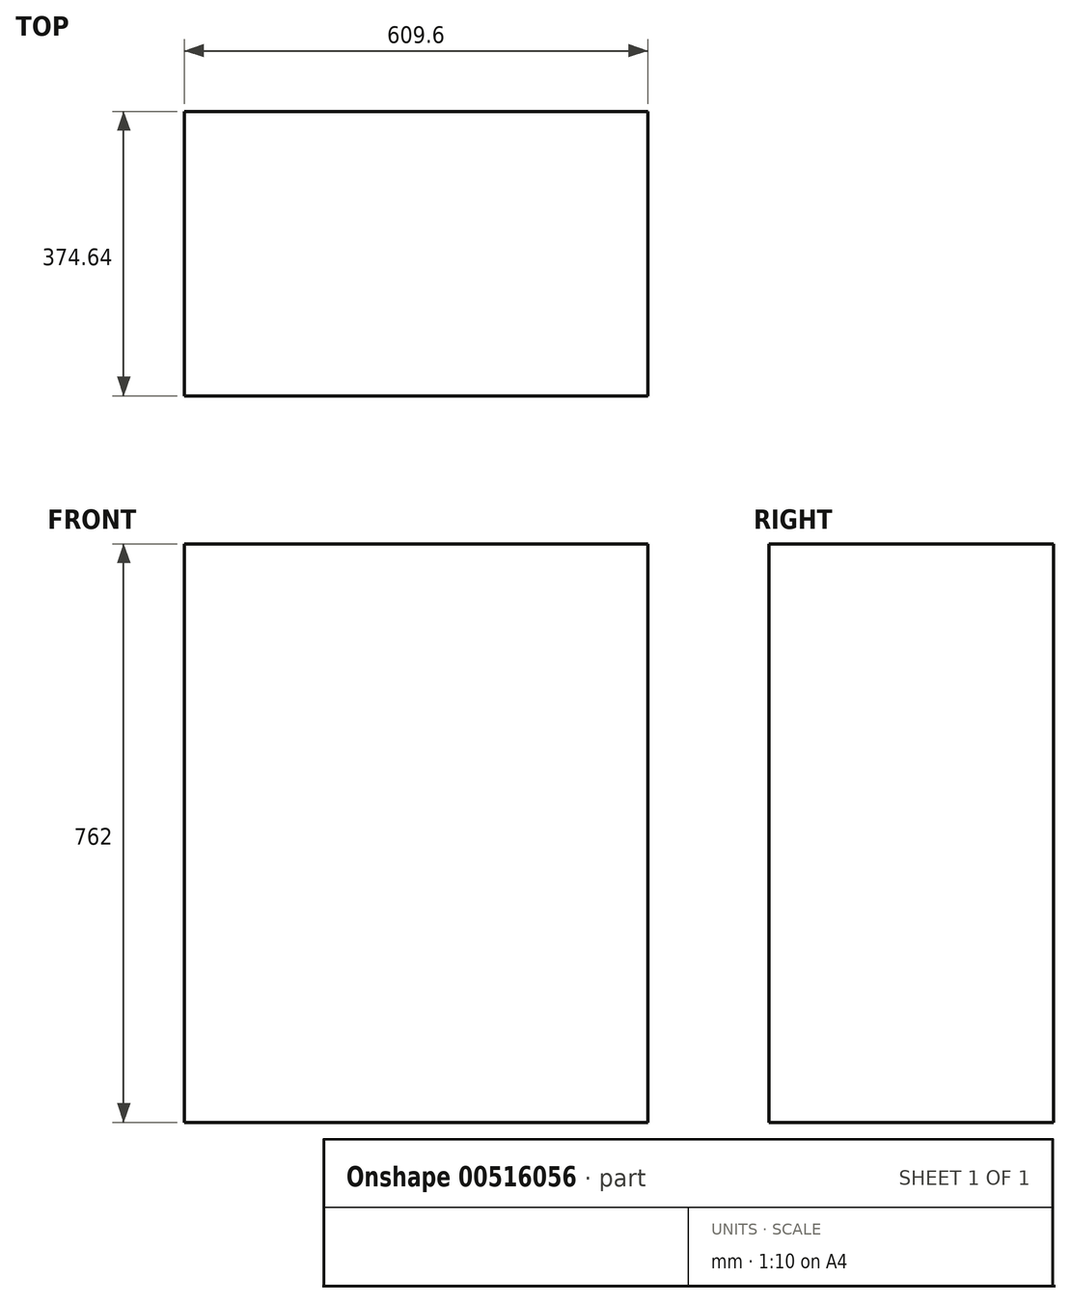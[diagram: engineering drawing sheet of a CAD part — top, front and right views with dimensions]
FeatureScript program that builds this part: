
annotation { "Feature Type Name" : "Feature", "Feature Type Description" : "" }
export const myFeature = defineFeature(function(context is Context, id is Id, definition is map)
    precondition{}
    {
        {
            var Q0;
            Q0=qCreatedBy(makeId("Top.planeOp"),FACE);
            var sketch = newSketch(context, id + "F0", { "sketchPlane" : qUnion([Q0])});
            skLineSegment(sketch, "E0.bottom", {"start": v(304.8, -187.32) * mm, "end": v(-304.8, -187.33) * mm});
            skLineSegment(sketch, "E0.top", {"start": v(304.8, 187.33) * mm, "end": v(-304.8, 187.32) * mm});
            skLineSegment(sketch, "E0.left", {"start": v(304.8, -187.32) * mm, "end": v(304.8, 187.33) * mm});
            skLineSegment(sketch, "E0.right", {"start": v(-304.8, -187.33) * mm, "end": v(-304.8, 187.32) * mm});
            skPoint(sketch, "E0.middle", {"position": v(0, 0) * mm});
            skSolve(sketch);
        }
        {
            var Q0;
            Q0=makeQuery(id+"F0.imprint","IMPRINT",FACE,{"disambiguationData":[TD([[makeQuery(id+"F0.imprint","IMPRINT",EDGE,{"derivedFrom":sQuery(id+"F0.wireOp",EDGE,"E0.bottom")}),-1.0]])]});
            extrude(context, id + "F1", {"entities" : qUnion([Q0]), "depth" : 762 * mm, "offsetDistance" : 25.4 * mm});
        }
    });
